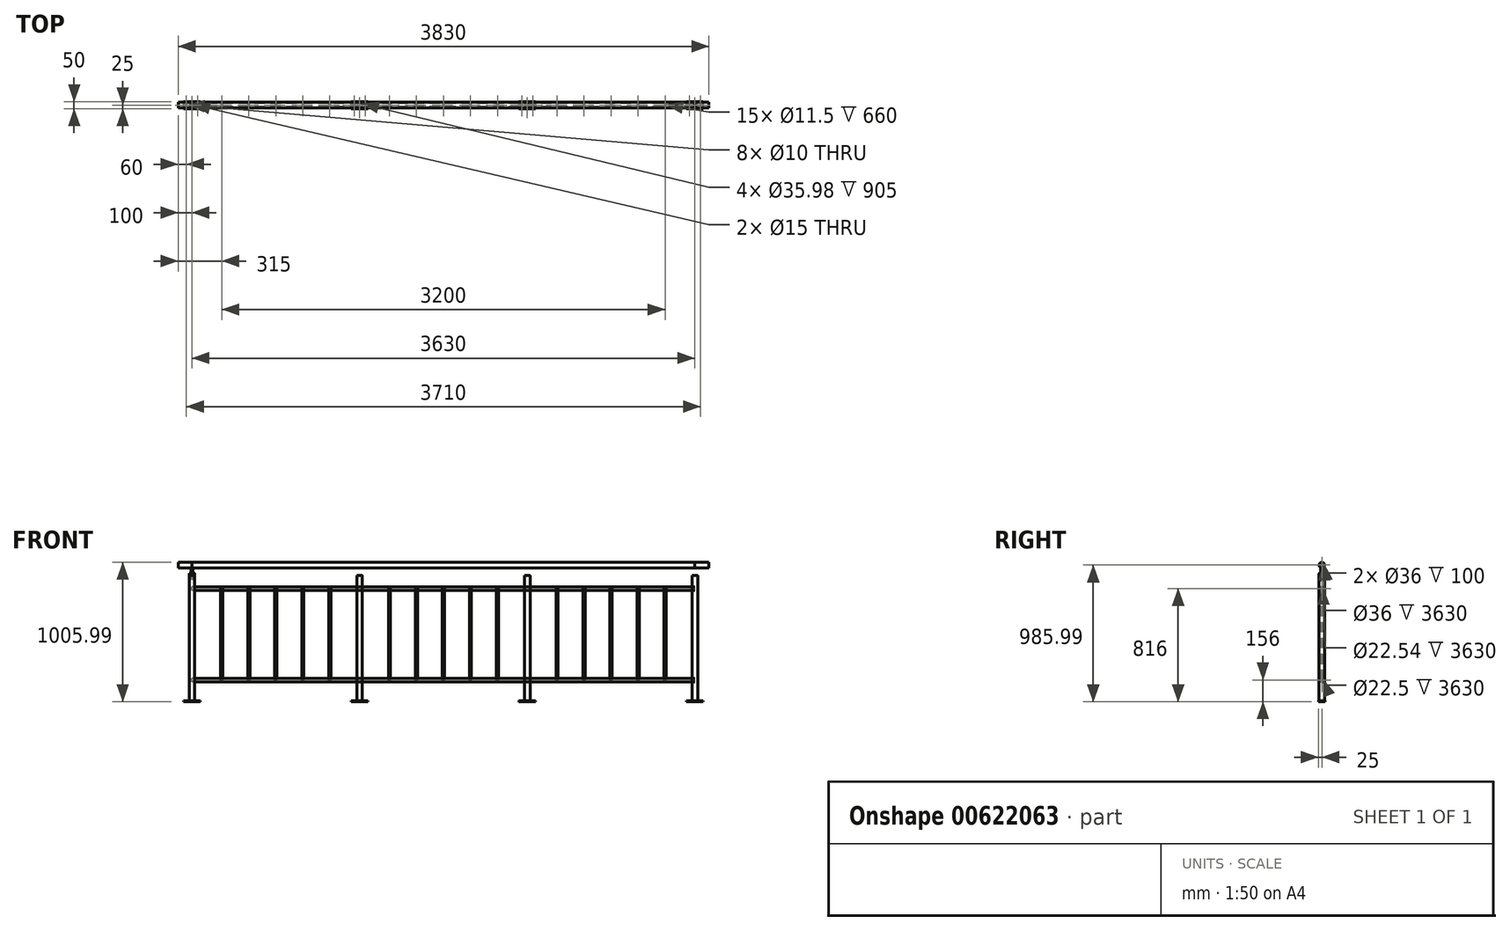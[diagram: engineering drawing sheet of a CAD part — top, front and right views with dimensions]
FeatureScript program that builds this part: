
annotation { "Feature Type Name" : "Feature", "Feature Type Description" : "" }
export const myFeature = defineFeature(function(context is Context, id is Id, definition is map)
    precondition{}
    {
        {
            var Q0;
            Q0=qCreatedBy(makeId("Top.planeOp"),FACE);
            var sketch = newSketch(context, id + "F0", { "sketchPlane" : qUnion([Q0])});
            skCircle(sketch, "E0", {"center": v(0, 0) * mm, "radius": 20 * mm});
            skCircle(sketch, "E1", {"center": v(0, 0) * mm, "radius": 17.99 * mm});
            skSolve(sketch);
        }
        {
            var Q0;
            Q0 = qSketchRegion(id + "F0", true);
            extrude(context, id + "F1", {"entities" : qUnion([Q0]), "oppositeDirection" : true, "depth" : 905 * mm, "offsetDistance" : 25 * mm});
        }
        {
            var Q0;
            Q0=qCreatedBy(makeId("Top.planeOp"),FACE);
            var sketch = newSketch(context, id + "F2", { "sketchPlane" : qUnion([Q0])});
            skCircle(sketch, "E2", {"center": v(0, 0) * mm, "radius": 17.98 * mm});
            skSolve(sketch);
        }
        {
            var Q0;
            Q0 = qSketchRegion(id + "F2", true);
            extrude(context, id + "F3", {"entities" : qUnion([Q0]), "oppositeDirection" : true, "depth" : 30 * mm, "offsetDistance" : 25 * mm});
        }
        {
            var Q0;
            Q0=makeQuery(id+"F3.opExtrude","CAP_FACE",FACE,{"disambiguationData":[OSD([sQuery(id+"F2.wireOp",EDGE,"E2")])],"isStart":true});
            var sketch = newSketch(context, id + "F4", { "sketchPlane" : qUnion([Q0])});
            skCircle(sketch, "E3", {"center": v(0, 0) * mm, "radius": 20 * mm});
            skSolve(sketch);
        }
        {
            var Q0;
            Q0 = qSketchRegion(id + "F4", true);
            extrude(context, id + "F5", {"entities" : qUnion([Q0]), "depth" : 15 * mm, "offsetDistance" : 25 * mm});
        }
        {
            var Q0;
            Q0=makeQuery(id+"F5.opExtrude","CAP_EDGE",EDGE,{"disambiguationData":[OSD([sQuery(id+"F4.wireOp",EDGE,"E3")])],"isStart":false});
            chamfer(context, id + "F6", {"entities" : qUnion([Q0]), "width" : 1 * mm, "tangentPropagation" : true});
        }
        {
            var Q0;
            Q0=makeQuery(id+"F5.opExtrude","CAP_FACE",FACE,{"disambiguationData":[OSD([sQuery(id+"F4.wireOp",EDGE,"E3")])],"isStart":false});
            var sketch = newSketch(context, id + "F7", { "sketchPlane" : qUnion([Q0])});
            skCircle(sketch, "E4", {"center": v(0, 0) * mm, "radius": 7.5 * mm});
            skSolve(sketch);
        }
        {
            var Q0;
            Q0 = qSketchRegion(id + "F7", true);
            extrude(context, id + "F8", {"entities" : qUnion([Q0]), "operationType" : NewBodyOperationType.REMOVE, "endBound" : BoundingType.THROUGH_ALL, "oppositeDirection" : true, "depth" : 25 * mm, "offsetDistance" : 25 * mm});
        }
        {
            var Q0;
            Q0=makeQuery(id+"F8.boolean.opBoolean","INTERSECT",EDGE,{"derivedFrom":[makeQuery(id+"F3.opExtrude","CAP_FACE",FACE,{"disambiguationData":[OSD([sQuery(id+"F2.wireOp",EDGE,"E2")])],"isStart":false}),makeQuery(id+"F8.opExtrude","SWEPT_FACE",FACE,{"disambiguationData":[OSD([sQuery(id+"F7.wireOp",EDGE,"E4")])]})]});
            chamfer(context, id + "F9", {"entities" : qUnion([Q0]), "width" : 3 * mm, "tangentPropagation" : true});
        }
        {
            var Q0;
            Q0=makeQuery(id+"F5.opExtrude","CAP_FACE",FACE,{"disambiguationData":[OSD([sQuery(id+"F4.wireOp",EDGE,"E3")])],"isStart":false});
            var sketch = newSketch(context, id + "F10", { "sketchPlane" : qUnion([Q0])});
            skCircle(sketch, "E5", {"center": v(0, 0) * mm, "radius": 7.5 * mm});
            skSolve(sketch);
        }
        {
            var Q0;
            Q0 = qSketchRegion(id + "F10", true);
            extrude(context, id + "F11", {"entities" : qUnion([Q0]), "depth" : 40 * mm, "offsetDistance" : 25 * mm});
        }
        {
            var Q0;
            Q0=makeQuery(id+"F11.opExtrude","CAP_FACE",FACE,{"disambiguationData":[OSD([sQuery(id+"F10.wireOp",EDGE,"E5")])],"isStart":true});
            var sketch = newSketch(context, id + "F12", { "sketchPlane" : qUnion([Q0])});
            skCircle(sketch, "E6", {"center": v(0, 0) * mm, "radius": 7.5 * mm});
            skSolve(sketch);
        }
        {
            var Q0;
            Q0 = qSketchRegion(id + "F12", true);
            extrude(context, id + "F13", {"entities" : qUnion([Q0]), "depth" : 35 * mm, "offsetDistance" : 25 * mm});
        }
        {
            var Q0;
            Q0=makeQuery(id+"F1.opExtrude","SWEPT_FACE",FACE,{"disambiguationData":[OSD([sQuery(id+"F0.wireOp",EDGE,"E0")])]});
            chamfer(context, id + "F14", {"entities" : qUnion([Q0]), "width" : 0.1 * mm, "tangentPropagation" : true});
        }
        {
            var Q0;
            Q0=makeQuery(id+"F5.opExtrude","CAP_FACE",FACE,{"disambiguationData":[OSD([sQuery(id+"F4.wireOp",EDGE,"E3")])],"isStart":true});
            chamfer(context, id + "F15", {"entities" : qUnion([Q0]), "width" : 0.1 * mm, "tangentPropagation" : true});
        }
        {
            var Q0;
            Q0=makeQuery(id+"F1.opExtrude","CAP_FACE",FACE,{"disambiguationData":[OSD([sQuery(id+"F0.wireOp",EDGE,"E0"),sQuery(id+"F0.wireOp",EDGE,"E1")])],"isStart":false});
            var sketch = newSketch(context, id + "F16", { "sketchPlane" : qUnion([Q0])});
            skLineSegment(sketch, "E7.bottom", {"start": v(60, -25) * mm, "end": v(-60, -25) * mm});
            skLineSegment(sketch, "E7.top", {"start": v(60, 25) * mm, "end": v(-60, 25) * mm});
            skLineSegment(sketch, "E7.left", {"start": v(60, -25) * mm, "end": v(60, 25) * mm});
            skLineSegment(sketch, "E7.right", {"start": v(-60, -25) * mm, "end": v(-60, 25) * mm});
            skPoint(sketch, "E7.middle", {"position": v(0, 0) * mm});
            skSolve(sketch);
        }
        {
            var Q0;
            Q0 = qSketchRegion(id + "F16", true);
            extrude(context, id + "F17", {"entities" : qUnion([Q0]), "operationType" : NewBodyOperationType.ADD, "depth" : 6 * mm, "offsetDistance" : 25 * mm});
        }
        {
            var Q0;
            Q0=makeQuery(id+"F17.opExtrude","CAP_FACE",FACE,{"disambiguationData":[OSD([sQuery(id+"F16.wireOp",EDGE,"E7.bottom"),sQuery(id+"F16.wireOp",EDGE,"E7.top"),sQuery(id+"F16.wireOp",EDGE,"E7.left"),sQuery(id+"F16.wireOp",EDGE,"E7.right")])],"isStart":false});
            var sketch = newSketch(context, id + "F18", { "sketchPlane" : qUnion([Q0])});
            skLineSegment(sketch, "E8", {"start": v(0, 0) * mm, "end": v(-20, 0) * mm, "construction": true});
            skLineSegment(sketch, "E9", {"start": v(-20, 0) * mm, "end": v(-40, 0) * mm, "construction": true});
            skLineSegment(sketch, "E10", {"start": v(-40, 0) * mm, "end": v(40, 0) * mm, "construction": true});
            skCircle(sketch, "E11", {"center": v(-40, 0) * mm, "radius": 5 * mm});
            skCircle(sketch, "E12", {"center": v(40, 0) * mm, "radius": 5 * mm});
            skSolve(sketch);
        }
        {
            var Q0;
            Q0 = qSketchRegion(id + "F18", true);
            extrude(context, id + "F19", {"entities" : qUnion([Q0]), "operationType" : NewBodyOperationType.REMOVE, "endBound" : BoundingType.THROUGH_ALL, "oppositeDirection" : true, "depth" : 25 * mm, "offsetDistance" : 25 * mm});
        }
        {
            var Q0;
            {var subQ0=sQuery(id+"F16.wireOp",EDGE,"E7.left");var subQ1=sQuery(id+"F16.wireOp",EDGE,"E7.top");var subQ3=sQuery(id+"F16.wireOp",EDGE,"E7.bottom");var subQ4=sQuery(id+"F16.wireOp",EDGE,"E7.right");Q0=makeQuery(id+"F19.boolean.opBoolean","INTERSECT",EDGE,{"derivedFrom":[makeQuery(id+"F17.boolean.opBoolean","SPLIT",FACE,{"disambiguationData":[TD([makeQuery(id+"F17.opExtrude","SWEPT_FACE",FACE,{"disambiguationData":[OSD([subQ3])]})])],"derivedFrom":makeQuery(id+"F17.opExtrude","CAP_FACE",FACE,{"disambiguationData":[OSD([subQ3,subQ1,subQ0,subQ4])],"isStart":true})}),makeQuery(id+"F19.opExtrude","SWEPT_FACE",FACE,{"disambiguationData":[OSD([sQuery(id+"F18.wireOp",EDGE,"E11")])]})]});}
            var Q1;
            {var subQ0=sQuery(id+"F16.wireOp",EDGE,"E7.left");var subQ1=sQuery(id+"F16.wireOp",EDGE,"E7.top");var subQ3=sQuery(id+"F16.wireOp",EDGE,"E7.bottom");var subQ4=sQuery(id+"F16.wireOp",EDGE,"E7.right");Q1=makeQuery(id+"F19.boolean.opBoolean","INTERSECT",EDGE,{"derivedFrom":[makeQuery(id+"F17.boolean.opBoolean","SPLIT",FACE,{"disambiguationData":[TD([makeQuery(id+"F17.opExtrude","SWEPT_FACE",FACE,{"disambiguationData":[OSD([subQ3])]})])],"derivedFrom":makeQuery(id+"F17.opExtrude","CAP_FACE",FACE,{"disambiguationData":[OSD([subQ3,subQ1,subQ0,subQ4])],"isStart":true})}),makeQuery(id+"F19.opExtrude","SWEPT_FACE",FACE,{"disambiguationData":[OSD([sQuery(id+"F18.wireOp",EDGE,"E12")])]})]});}
            chamfer(context, id + "F20", {"entities" : qUnion([Q0, Q1]), "width" : 2 * mm, "tangentPropagation" : true});
        }
        {
            var Q0;
            Q0=makeQuery(id+"F17.opExtrude","CAP_EDGE",EDGE,{"disambiguationData":[OSD([sQuery(id+"F16.wireOp",EDGE,"E7.right")])],"isStart":true});
            var Q1;
            Q1=makeQuery(id+"F17.opExtrude","CAP_EDGE",EDGE,{"disambiguationData":[OSD([sQuery(id+"F16.wireOp",EDGE,"E7.top")])],"isStart":true});
            var Q2;
            Q2=makeQuery(id+"F17.opExtrude","CAP_EDGE",EDGE,{"disambiguationData":[OSD([sQuery(id+"F16.wireOp",EDGE,"E7.bottom")])],"isStart":true});
            var Q3;
            Q3=makeQuery(id+"F17.opExtrude","CAP_EDGE",EDGE,{"disambiguationData":[OSD([sQuery(id+"F16.wireOp",EDGE,"E7.left")])],"isStart":true});
            chamfer(context, id + "F21", {"entities" : qUnion([Q0, Q1, Q2, Q3]), "width" : 1 * mm, "tangentPropagation" : true});
        }
        {
            var Q0;
            Q0=makeQuery(id+"F1.opExtrude","SWEPT_BODY",BODY,{"disambiguationData":[OSD([sQuery(id+"F0.wireOp",EDGE,"E0"),sQuery(id+"F0.wireOp",EDGE,"E1")])]});
            transform(context, id + "F22", {"entities" : qUnion([Q0]), "transformType" : TransformType.TRANSLATION_3D, "dx" : 1210 * mm, "dy" : 0 * mm, "dz" : 0 * mm, "makeCopy" : true});
        }
        {
            var Q0;
            Q0=makeQuery(id+"F22.opPattern","COPY",BODY,{"derivedFrom":makeQuery(id+"F1.opExtrude","SWEPT_BODY",BODY,{"disambiguationData":[OSD([sQuery(id+"F0.wireOp",EDGE,"E0"),sQuery(id+"F0.wireOp",EDGE,"E1")])]}),"instanceName":"1"});
            transform(context, id + "F23", {"entities" : qUnion([Q0]), "transformType" : TransformType.TRANSLATION_3D, "dx" : 1210 * mm, "dy" : 0 * mm, "dz" : 0 * mm, "makeCopy" : true});
        }
        {
            var Q0;
            Q0=makeQuery(id+"F23.opPattern","COPY",BODY,{"derivedFrom":makeQuery(id+"F22.opPattern","COPY",BODY,{"derivedFrom":makeQuery(id+"F1.opExtrude","SWEPT_BODY",BODY,{"disambiguationData":[OSD([sQuery(id+"F0.wireOp",EDGE,"E0"),sQuery(id+"F0.wireOp",EDGE,"E1")])]}),"instanceName":"1"}),"instanceName":"1"});
            transform(context, id + "F24", {"entities" : qUnion([Q0]), "transformType" : TransformType.TRANSLATION_3D, "dx" : 1210 * mm, "dy" : 0 * mm, "dz" : 0 * mm, "makeCopy" : true});
        }
        {
            var Q0;
            Q0=qCreatedBy(makeId("Right.planeOp"),FACE);
            var sketch = newSketch(context, id + "F25", { "sketchPlane" : qUnion([Q0])});
            skLineSegment(sketch, "E13", {"start": v(0, 0) * mm, "end": v(0, 55) * mm, "construction": true});
            skLineSegment(sketch, "E14", {"start": v(0, 55) * mm, "end": v(0, 75) * mm, "construction": true});
            skCircle(sketch, "E15", {"center": v(0, 75) * mm, "radius": 20 * mm});
            skCircle(sketch, "E16", {"center": v(0, 75) * mm, "radius": 18 * mm});
            skSolve(sketch);
        }
        {
            var Q0;
            Q0 = qSketchRegion(id + "F25", true);
            extrude(context, id + "F26", {"entities" : qUnion([Q0]), "depth" : 3630 * mm, "offsetDistance" : 25 * mm});
        }
        {
            var Q0;
            Q0=makeQuery(id+"F26.opExtrude","CAP_FACE",FACE,{"disambiguationData":[OSD([sQuery(id+"F25.wireOp",EDGE,"E15"),sQuery(id+"F25.wireOp",EDGE,"E16")])],"isStart":false});
            var sketch = newSketch(context, id + "F27", { "sketchPlane" : qUnion([Q0])});
            skCircle(sketch, "E17", {"center": v(0, 75) * mm, "radius": 20 * mm});
            skCircle(sketch, "E18", {"center": v(0, 75) * mm, "radius": 18 * mm});
            skSolve(sketch);
        }
        {
            var Q0;
            Q0 = qSketchRegion(id + "F27", true);
            extrude(context, id + "F28", {"entities" : qUnion([Q0]), "depth" : 100 * mm, "offsetDistance" : 25 * mm});
        }
        {
            var Q0;
            Q0=makeQuery(id+"F26.opExtrude","CAP_FACE",FACE,{"disambiguationData":[OSD([sQuery(id+"F25.wireOp",EDGE,"E15"),sQuery(id+"F25.wireOp",EDGE,"E16")])],"isStart":true});
            var sketch = newSketch(context, id + "F29", { "sketchPlane" : qUnion([Q0])});
            skCircle(sketch, "E19", {"center": v(0, 75) * mm, "radius": 20 * mm});
            skCircle(sketch, "E20", {"center": v(0, 75) * mm, "radius": 18 * mm});
            skSolve(sketch);
        }
        {
            var Q0;
            Q0 = qSketchRegion(id + "F29", true);
            extrude(context, id + "F30", {"entities" : qUnion([Q0]), "depth" : 100 * mm, "offsetDistance" : 25 * mm});
        }
        {
            var Q0;
            Q0=qCreatedBy(makeId("Right.planeOp"),FACE);
            var sketch = newSketch(context, id + "F31", { "sketchPlane" : qUnion([Q0])});
            skLineSegment(sketch, "E21", {"start": v(0, 0) * mm, "end": v(0, -95) * mm, "construction": true});
            skCircle(sketch, "E22", {"center": v(0, -95) * mm, "radius": 13.45 * mm});
            skCircle(sketch, "E23", {"center": v(0, -95) * mm, "radius": 11.27 * mm});
            skSolve(sketch);
        }
        {
            var Q0;
            Q0 = qSketchRegion(id + "F31", true);
            extrude(context, id + "F32", {"entities" : qUnion([Q0]), "depth" : 3630 * mm, "offsetDistance" : 25 * mm});
        }
        {
            var Q0;
            Q0=qCreatedBy(makeId("Right.planeOp"),FACE);
            var sketch = newSketch(context, id + "F33", { "sketchPlane" : qUnion([Q0])});
            skLineSegment(sketch, "E24", {"start": v(0, 0) * mm, "end": v(0, -905) * mm, "construction": true});
            skLineSegment(sketch, "E25", {"start": v(0, -905) * mm, "end": v(0, -755) * mm, "construction": true});
            skCircle(sketch, "E26", {"center": v(0, -755) * mm, "radius": 13.45 * mm});
            skCircle(sketch, "E27", {"center": v(0, -755) * mm, "radius": 11.25 * mm});
            skSolve(sketch);
        }
        {
            var Q0;
            Q0 = qSketchRegion(id + "F33", true);
            extrude(context, id + "F34", {"entities" : qUnion([Q0]), "depth" : 3630 * mm, "offsetDistance" : 25 * mm});
        }
        {
            var Q0;
            Q0=qCreatedBy(makeId("Top.planeOp"),FACE);
            var sketch = newSketch(context, id + "F35", { "sketchPlane" : qUnion([Q0])});
            skLineSegment(sketch, "E28", {"start": v(0, 0) * mm, "end": v(20, 0) * mm, "construction": true});
            skLineSegment(sketch, "E29", {"start": v(20, 0) * mm, "end": v(215, 0) * mm, "construction": true});
            skCircle(sketch, "E30", {"center": v(215, 0) * mm, "radius": 7.5 * mm});
            skSolve(sketch);
        }
        {
            var Q0;
            Q0 = qSketchRegion(id + "F35", true);
            extrude(context, id + "F36", {"entities" : qUnion([Q0]), "operationType" : NewBodyOperationType.ADD, "oppositeDirection" : true, "depth" : 40 * mm, "offsetDistance" : 25 * mm});
        }
        {
            var Q0;
            Q0=makeQuery(id+"F36.opExtrude","CAP_FACE",FACE,{"disambiguationData":[OSD([sQuery(id+"F35.wireOp",EDGE,"E30")])],"isStart":false});
            var sketch = newSketch(context, id + "F37", { "sketchPlane" : qUnion([Q0])});
            skCircle(sketch, "E31", {"center": v(215, 0) * mm, "radius": 7.5 * mm});
            skSolve(sketch);
        }
        {
            var Q0;
            Q0 = qSketchRegion(id + "F37", true);
            extrude(context, id + "F38", {"entities" : qUnion([Q0]), "depth" : 55 * mm, "offsetDistance" : 25 * mm});
        }
        {
            var Q0;
            Q0=makeQuery(id+"F38.opExtrude","CAP_FACE",FACE,{"disambiguationData":[OSD([sQuery(id+"F37.wireOp",EDGE,"E31")])],"isStart":false});
            var sketch = newSketch(context, id + "F39", { "sketchPlane" : qUnion([Q0])});
            skCircle(sketch, "E32", {"center": v(215, 0) * mm, "radius": 7.5 * mm});
            skCircle(sketch, "E33", {"center": v(215, 0) * mm, "radius": 5.75 * mm});
            skSolve(sketch);
        }
        {
            var Q0;
            Q0 = qSketchRegion(id + "F39", true);
            extrude(context, id + "F40", {"entities" : qUnion([Q0]), "depth" : 660 * mm, "offsetDistance" : 25 * mm});
        }
        {
            var Q0;
            Q0=makeQuery(id+"F36.opExtrude","SWEPT_BODY",BODY,{"disambiguationData":[OSD([sQuery(id+"F35.wireOp",EDGE,"E30")])]});
            deleteBodies(context, id + "F41", {"entities" : qUnion([Q0])});
        }
        {
            var Q0;
            Q0=makeQuery(id+"F38.opExtrude","SWEPT_BODY",BODY,{"disambiguationData":[OSD([sQuery(id+"F37.wireOp",EDGE,"E31")])]});
            deleteBodies(context, id + "F42", {"entities" : qUnion([Q0])});
        }
        {
            var Q0;
            Q0=makeQuery(id+"F40.opExtrude","SWEPT_BODY",BODY,{"disambiguationData":[OSD([sQuery(id+"F39.wireOp",EDGE,"E32"),sQuery(id+"F39.wireOp",EDGE,"E33")])]});
            transform(context, id + "F43", {"entities" : qUnion([Q0]), "transformType" : TransformType.TRANSLATION_3D, "dx" : 195 * mm, "dy" : 0 * mm, "dz" : 0 * mm, "makeCopy" : true});
        }
        {
            var Q0;
            Q0=makeQuery(id+"F43.opPattern","COPY",BODY,{"derivedFrom":makeQuery(id+"F40.opExtrude","SWEPT_BODY",BODY,{"disambiguationData":[OSD([sQuery(id+"F39.wireOp",EDGE,"E32"),sQuery(id+"F39.wireOp",EDGE,"E33")])]}),"instanceName":"1"});
            transform(context, id + "F44", {"entities" : qUnion([Q0]), "transformType" : TransformType.TRANSLATION_3D, "dx" : 195 * mm, "dy" : 0 * mm, "dz" : 0 * mm, "makeCopy" : true});
        }
        {
            var Q0;
            Q0=makeQuery(id+"F44.opPattern","COPY",BODY,{"derivedFrom":makeQuery(id+"F43.opPattern","COPY",BODY,{"derivedFrom":makeQuery(id+"F40.opExtrude","SWEPT_BODY",BODY,{"disambiguationData":[OSD([sQuery(id+"F39.wireOp",EDGE,"E32"),sQuery(id+"F39.wireOp",EDGE,"E33")])]}),"instanceName":"1"}),"instanceName":"1"});
            transform(context, id + "F45", {"entities" : qUnion([Q0]), "transformType" : TransformType.TRANSLATION_3D, "dx" : 195 * mm, "dy" : 0 * mm, "dz" : 0 * mm, "makeCopy" : true});
        }
        {
            var Q0;
            Q0=makeQuery(id+"F45.opPattern","COPY",BODY,{"derivedFrom":makeQuery(id+"F44.opPattern","COPY",BODY,{"derivedFrom":makeQuery(id+"F43.opPattern","COPY",BODY,{"derivedFrom":makeQuery(id+"F40.opExtrude","SWEPT_BODY",BODY,{"disambiguationData":[OSD([sQuery(id+"F39.wireOp",EDGE,"E32"),sQuery(id+"F39.wireOp",EDGE,"E33")])]}),"instanceName":"1"}),"instanceName":"1"}),"instanceName":"1"});
            transform(context, id + "F46", {"entities" : qUnion([Q0]), "transformType" : TransformType.TRANSLATION_3D, "dx" : 195 * mm, "dy" : 0 * mm, "dz" : 0 * mm, "makeCopy" : true});
        }
        {
            var Q0;
            Q0=makeQuery(id+"F46.opPattern","COPY",BODY,{"derivedFrom":makeQuery(id+"F45.opPattern","COPY",BODY,{"derivedFrom":makeQuery(id+"F44.opPattern","COPY",BODY,{"derivedFrom":makeQuery(id+"F43.opPattern","COPY",BODY,{"derivedFrom":makeQuery(id+"F40.opExtrude","SWEPT_BODY",BODY,{"disambiguationData":[OSD([sQuery(id+"F39.wireOp",EDGE,"E32"),sQuery(id+"F39.wireOp",EDGE,"E33")])]}),"instanceName":"1"}),"instanceName":"1"}),"instanceName":"1"}),"instanceName":"1"});
            transform(context, id + "F47", {"entities" : qUnion([Q0]), "transformType" : TransformType.TRANSLATION_3D, "dx" : 430 * mm, "dy" : 0 * mm, "dz" : 0 * mm, "makeCopy" : true});
        }
        {
            var Q0;
            Q0=makeQuery(id+"F47.opPattern","COPY",BODY,{"derivedFrom":makeQuery(id+"F46.opPattern","COPY",BODY,{"derivedFrom":makeQuery(id+"F45.opPattern","COPY",BODY,{"derivedFrom":makeQuery(id+"F44.opPattern","COPY",BODY,{"derivedFrom":makeQuery(id+"F43.opPattern","COPY",BODY,{"derivedFrom":makeQuery(id+"F40.opExtrude","SWEPT_BODY",BODY,{"disambiguationData":[OSD([sQuery(id+"F39.wireOp",EDGE,"E32"),sQuery(id+"F39.wireOp",EDGE,"E33")])]}),"instanceName":"1"}),"instanceName":"1"}),"instanceName":"1"}),"instanceName":"1"}),"instanceName":"1"});
            transform(context, id + "F48", {"entities" : qUnion([Q0]), "transformType" : TransformType.TRANSLATION_3D, "dx" : 195 * mm, "dy" : 0 * mm, "dz" : 0 * mm, "makeCopy" : true});
        }
        {
            var Q0;
            Q0=makeQuery(id+"F48.opPattern","COPY",BODY,{"derivedFrom":makeQuery(id+"F47.opPattern","COPY",BODY,{"derivedFrom":makeQuery(id+"F46.opPattern","COPY",BODY,{"derivedFrom":makeQuery(id+"F45.opPattern","COPY",BODY,{"derivedFrom":makeQuery(id+"F44.opPattern","COPY",BODY,{"derivedFrom":makeQuery(id+"F43.opPattern","COPY",BODY,{"derivedFrom":makeQuery(id+"F40.opExtrude","SWEPT_BODY",BODY,{"disambiguationData":[OSD([sQuery(id+"F39.wireOp",EDGE,"E32"),sQuery(id+"F39.wireOp",EDGE,"E33")])]}),"instanceName":"1"}),"instanceName":"1"}),"instanceName":"1"}),"instanceName":"1"}),"instanceName":"1"}),"instanceName":"1"});
            transform(context, id + "F49", {"entities" : qUnion([Q0]), "transformType" : TransformType.TRANSLATION_3D, "dx" : 195 * mm, "dy" : 0 * mm, "dz" : 0 * mm, "makeCopy" : true});
        }
        {
            var Q0;
            Q0=makeQuery(id+"F49.opPattern","COPY",BODY,{"derivedFrom":makeQuery(id+"F48.opPattern","COPY",BODY,{"derivedFrom":makeQuery(id+"F47.opPattern","COPY",BODY,{"derivedFrom":makeQuery(id+"F46.opPattern","COPY",BODY,{"derivedFrom":makeQuery(id+"F45.opPattern","COPY",BODY,{"derivedFrom":makeQuery(id+"F44.opPattern","COPY",BODY,{"derivedFrom":makeQuery(id+"F43.opPattern","COPY",BODY,{"derivedFrom":makeQuery(id+"F40.opExtrude","SWEPT_BODY",BODY,{"disambiguationData":[OSD([sQuery(id+"F39.wireOp",EDGE,"E32"),sQuery(id+"F39.wireOp",EDGE,"E33")])]}),"instanceName":"1"}),"instanceName":"1"}),"instanceName":"1"}),"instanceName":"1"}),"instanceName":"1"}),"instanceName":"1"}),"instanceName":"1"});
            transform(context, id + "F50", {"entities" : qUnion([Q0]), "transformType" : TransformType.TRANSLATION_3D, "dx" : 195 * mm, "dy" : 0 * mm, "dz" : 0 * mm, "makeCopy" : true});
        }
        {
            var Q0;
            Q0=makeQuery(id+"F50.opPattern","COPY",BODY,{"derivedFrom":makeQuery(id+"F49.opPattern","COPY",BODY,{"derivedFrom":makeQuery(id+"F48.opPattern","COPY",BODY,{"derivedFrom":makeQuery(id+"F47.opPattern","COPY",BODY,{"derivedFrom":makeQuery(id+"F46.opPattern","COPY",BODY,{"derivedFrom":makeQuery(id+"F45.opPattern","COPY",BODY,{"derivedFrom":makeQuery(id+"F44.opPattern","COPY",BODY,{"derivedFrom":makeQuery(id+"F43.opPattern","COPY",BODY,{"derivedFrom":makeQuery(id+"F40.opExtrude","SWEPT_BODY",BODY,{"disambiguationData":[OSD([sQuery(id+"F39.wireOp",EDGE,"E32"),sQuery(id+"F39.wireOp",EDGE,"E33")])]}),"instanceName":"1"}),"instanceName":"1"}),"instanceName":"1"}),"instanceName":"1"}),"instanceName":"1"}),"instanceName":"1"}),"instanceName":"1"}),"instanceName":"1"});
            transform(context, id + "F51", {"entities" : qUnion([Q0]), "transformType" : TransformType.TRANSLATION_3D, "dx" : 195 * mm, "dy" : 0 * mm, "dz" : 0 * mm, "makeCopy" : true});
        }
        {
            var Q0;
            Q0=makeQuery(id+"F51.opPattern","COPY",BODY,{"derivedFrom":makeQuery(id+"F50.opPattern","COPY",BODY,{"derivedFrom":makeQuery(id+"F49.opPattern","COPY",BODY,{"derivedFrom":makeQuery(id+"F48.opPattern","COPY",BODY,{"derivedFrom":makeQuery(id+"F47.opPattern","COPY",BODY,{"derivedFrom":makeQuery(id+"F46.opPattern","COPY",BODY,{"derivedFrom":makeQuery(id+"F45.opPattern","COPY",BODY,{"derivedFrom":makeQuery(id+"F44.opPattern","COPY",BODY,{"derivedFrom":makeQuery(id+"F43.opPattern","COPY",BODY,{"derivedFrom":makeQuery(id+"F40.opExtrude","SWEPT_BODY",BODY,{"disambiguationData":[OSD([sQuery(id+"F39.wireOp",EDGE,"E32"),sQuery(id+"F39.wireOp",EDGE,"E33")])]}),"instanceName":"1"}),"instanceName":"1"}),"instanceName":"1"}),"instanceName":"1"}),"instanceName":"1"}),"instanceName":"1"}),"instanceName":"1"}),"instanceName":"1"}),"instanceName":"1"});
            transform(context, id + "F52", {"entities" : qUnion([Q0]), "transformType" : TransformType.TRANSLATION_3D, "dx" : 430 * mm, "dy" : 0 * mm, "dz" : 0 * mm, "makeCopy" : true});
        }
        {
            var Q0;
            Q0=makeQuery(id+"F52.opPattern","COPY",BODY,{"derivedFrom":makeQuery(id+"F51.opPattern","COPY",BODY,{"derivedFrom":makeQuery(id+"F50.opPattern","COPY",BODY,{"derivedFrom":makeQuery(id+"F49.opPattern","COPY",BODY,{"derivedFrom":makeQuery(id+"F48.opPattern","COPY",BODY,{"derivedFrom":makeQuery(id+"F47.opPattern","COPY",BODY,{"derivedFrom":makeQuery(id+"F46.opPattern","COPY",BODY,{"derivedFrom":makeQuery(id+"F45.opPattern","COPY",BODY,{"derivedFrom":makeQuery(id+"F44.opPattern","COPY",BODY,{"derivedFrom":makeQuery(id+"F43.opPattern","COPY",BODY,{"derivedFrom":makeQuery(id+"F40.opExtrude","SWEPT_BODY",BODY,{"disambiguationData":[OSD([sQuery(id+"F39.wireOp",EDGE,"E32"),sQuery(id+"F39.wireOp",EDGE,"E33")])]}),"instanceName":"1"}),"instanceName":"1"}),"instanceName":"1"}),"instanceName":"1"}),"instanceName":"1"}),"instanceName":"1"}),"instanceName":"1"}),"instanceName":"1"}),"instanceName":"1"}),"instanceName":"1"});
            transform(context, id + "F53", {"entities" : qUnion([Q0]), "transformType" : TransformType.TRANSLATION_3D, "dx" : 195 * mm, "dy" : 0 * mm, "dz" : 0 * mm, "makeCopy" : true});
        }
        {
            var Q0;
            Q0=makeQuery(id+"F53.opPattern","COPY",BODY,{"derivedFrom":makeQuery(id+"F52.opPattern","COPY",BODY,{"derivedFrom":makeQuery(id+"F51.opPattern","COPY",BODY,{"derivedFrom":makeQuery(id+"F50.opPattern","COPY",BODY,{"derivedFrom":makeQuery(id+"F49.opPattern","COPY",BODY,{"derivedFrom":makeQuery(id+"F48.opPattern","COPY",BODY,{"derivedFrom":makeQuery(id+"F47.opPattern","COPY",BODY,{"derivedFrom":makeQuery(id+"F46.opPattern","COPY",BODY,{"derivedFrom":makeQuery(id+"F45.opPattern","COPY",BODY,{"derivedFrom":makeQuery(id+"F44.opPattern","COPY",BODY,{"derivedFrom":makeQuery(id+"F43.opPattern","COPY",BODY,{"derivedFrom":makeQuery(id+"F40.opExtrude","SWEPT_BODY",BODY,{"disambiguationData":[OSD([sQuery(id+"F39.wireOp",EDGE,"E32"),sQuery(id+"F39.wireOp",EDGE,"E33")])]}),"instanceName":"1"}),"instanceName":"1"}),"instanceName":"1"}),"instanceName":"1"}),"instanceName":"1"}),"instanceName":"1"}),"instanceName":"1"}),"instanceName":"1"}),"instanceName":"1"}),"instanceName":"1"}),"instanceName":"1"});
            transform(context, id + "F54", {"entities" : qUnion([Q0]), "transformType" : TransformType.TRANSLATION_3D, "dx" : 195 * mm, "dy" : 0 * mm, "dz" : 0 * mm, "makeCopy" : true});
        }
        {
            var Q0;
            Q0=makeQuery(id+"F54.opPattern","COPY",BODY,{"derivedFrom":makeQuery(id+"F53.opPattern","COPY",BODY,{"derivedFrom":makeQuery(id+"F52.opPattern","COPY",BODY,{"derivedFrom":makeQuery(id+"F51.opPattern","COPY",BODY,{"derivedFrom":makeQuery(id+"F50.opPattern","COPY",BODY,{"derivedFrom":makeQuery(id+"F49.opPattern","COPY",BODY,{"derivedFrom":makeQuery(id+"F48.opPattern","COPY",BODY,{"derivedFrom":makeQuery(id+"F47.opPattern","COPY",BODY,{"derivedFrom":makeQuery(id+"F46.opPattern","COPY",BODY,{"derivedFrom":makeQuery(id+"F45.opPattern","COPY",BODY,{"derivedFrom":makeQuery(id+"F44.opPattern","COPY",BODY,{"derivedFrom":makeQuery(id+"F43.opPattern","COPY",BODY,{"derivedFrom":makeQuery(id+"F40.opExtrude","SWEPT_BODY",BODY,{"disambiguationData":[OSD([sQuery(id+"F39.wireOp",EDGE,"E32"),sQuery(id+"F39.wireOp",EDGE,"E33")])]}),"instanceName":"1"}),"instanceName":"1"}),"instanceName":"1"}),"instanceName":"1"}),"instanceName":"1"}),"instanceName":"1"}),"instanceName":"1"}),"instanceName":"1"}),"instanceName":"1"}),"instanceName":"1"}),"instanceName":"1"}),"instanceName":"1"});
            transform(context, id + "F55", {"entities" : qUnion([Q0]), "transformType" : TransformType.TRANSLATION_3D, "dx" : 195 * mm, "dy" : 0 * mm, "dz" : 0 * mm, "makeCopy" : true});
        }
        {
            var Q0;
            Q0=makeQuery(id+"F55.opPattern","COPY",BODY,{"derivedFrom":makeQuery(id+"F54.opPattern","COPY",BODY,{"derivedFrom":makeQuery(id+"F53.opPattern","COPY",BODY,{"derivedFrom":makeQuery(id+"F52.opPattern","COPY",BODY,{"derivedFrom":makeQuery(id+"F51.opPattern","COPY",BODY,{"derivedFrom":makeQuery(id+"F50.opPattern","COPY",BODY,{"derivedFrom":makeQuery(id+"F49.opPattern","COPY",BODY,{"derivedFrom":makeQuery(id+"F48.opPattern","COPY",BODY,{"derivedFrom":makeQuery(id+"F47.opPattern","COPY",BODY,{"derivedFrom":makeQuery(id+"F46.opPattern","COPY",BODY,{"derivedFrom":makeQuery(id+"F45.opPattern","COPY",BODY,{"derivedFrom":makeQuery(id+"F44.opPattern","COPY",BODY,{"derivedFrom":makeQuery(id+"F43.opPattern","COPY",BODY,{"derivedFrom":makeQuery(id+"F40.opExtrude","SWEPT_BODY",BODY,{"disambiguationData":[OSD([sQuery(id+"F39.wireOp",EDGE,"E32"),sQuery(id+"F39.wireOp",EDGE,"E33")])]}),"instanceName":"1"}),"instanceName":"1"}),"instanceName":"1"}),"instanceName":"1"}),"instanceName":"1"}),"instanceName":"1"}),"instanceName":"1"}),"instanceName":"1"}),"instanceName":"1"}),"instanceName":"1"}),"instanceName":"1"}),"instanceName":"1"}),"instanceName":"1"});
            transform(context, id + "F56", {"entities" : qUnion([Q0]), "transformType" : TransformType.TRANSLATION_3D, "dx" : 195 * mm, "dy" : 0 * mm, "dz" : 0 * mm, "makeCopy" : true});
        }
    });
